# Revit family: Gira_129600
name_source: partatom
category: Elektroinstallationen
revit_build: Autodesk Revit 2017 (Build: 20160225_1515(x64)
units: mm (PartAtom-declared; Revit-internal decimal feet)

## family parameters
Basisbauteil = Fläche
Beim Laden mit Abzugskörper schneiden = Nein
Bemaßung runder Anschluss = Durchmesser verwenden
Beschriftungsausrichtung beibehalten = Nein
Gemeinsam genutzt = Nein
Raumberechnungspunkt = Nein
Teiletyp = Normal

## types (1)
- Spannungsversorgung DC 24 V 300 mA REG Türko
    Anwendung = sonstige
    Ausgangsspannung [Volt] = 24
    Auswertefunktion = Nein
    BIM = https://media.live.bim.site 00_REG 6.rfa
    BIMSITE_PRODUCT_ID = 21df1e56c7accd880677f37bc9f96e8d9aef7743
    Beschreibung = Spannungsversorgung für Türkommunikation DC 24 V 300 mA  REG Merkmale:  Spannungsversorgung DC 24 V zur Versorgung von Türkommunikations-Komponenten.  Versorgung der Farbkamera in großen Objekten.  Versorgung der Ruftastenausleuchtung in großen Objekten.  Versorgung des TKS-TK-Gateways, wenn das Steuergerät Video verwendet wird.  Versorgung von Keyless In Codetastatur.
    Datenblatt = https://media.live.bim.site
    Datenblatt 1 = https://media.live.bim.site
    Eingangsspannung [Volt] = 230
    GTIN = 4010337296003
    HAN = 129600
    HeinzeBIM = https://www.heinze.de
    Hersteller = Gira
    Installationstechnik = Bus-System
    Integrierte Türöffnerschaltung = Nein
    Ist System = Nein
    Ist Zubehör = Nein
    Kosten = 0 $
    Produktseite = https://media.live.bim.site
    Programmiersperre = Nein
    Schutzart (IP) = IP20
    Serviceanzeigen = Nein
    Steuerfunktion = Nein
    Stromart = DC
    Typname = Spannungsversorgung DC 24 V 300 mA REG Türko
    URL = https://www.gira.de
    Vorgabe-Ansicht = 1219 mm

## geometry (parser evidence)
native form markers: Sweep x2
no freeform markers — native parametric forms only
